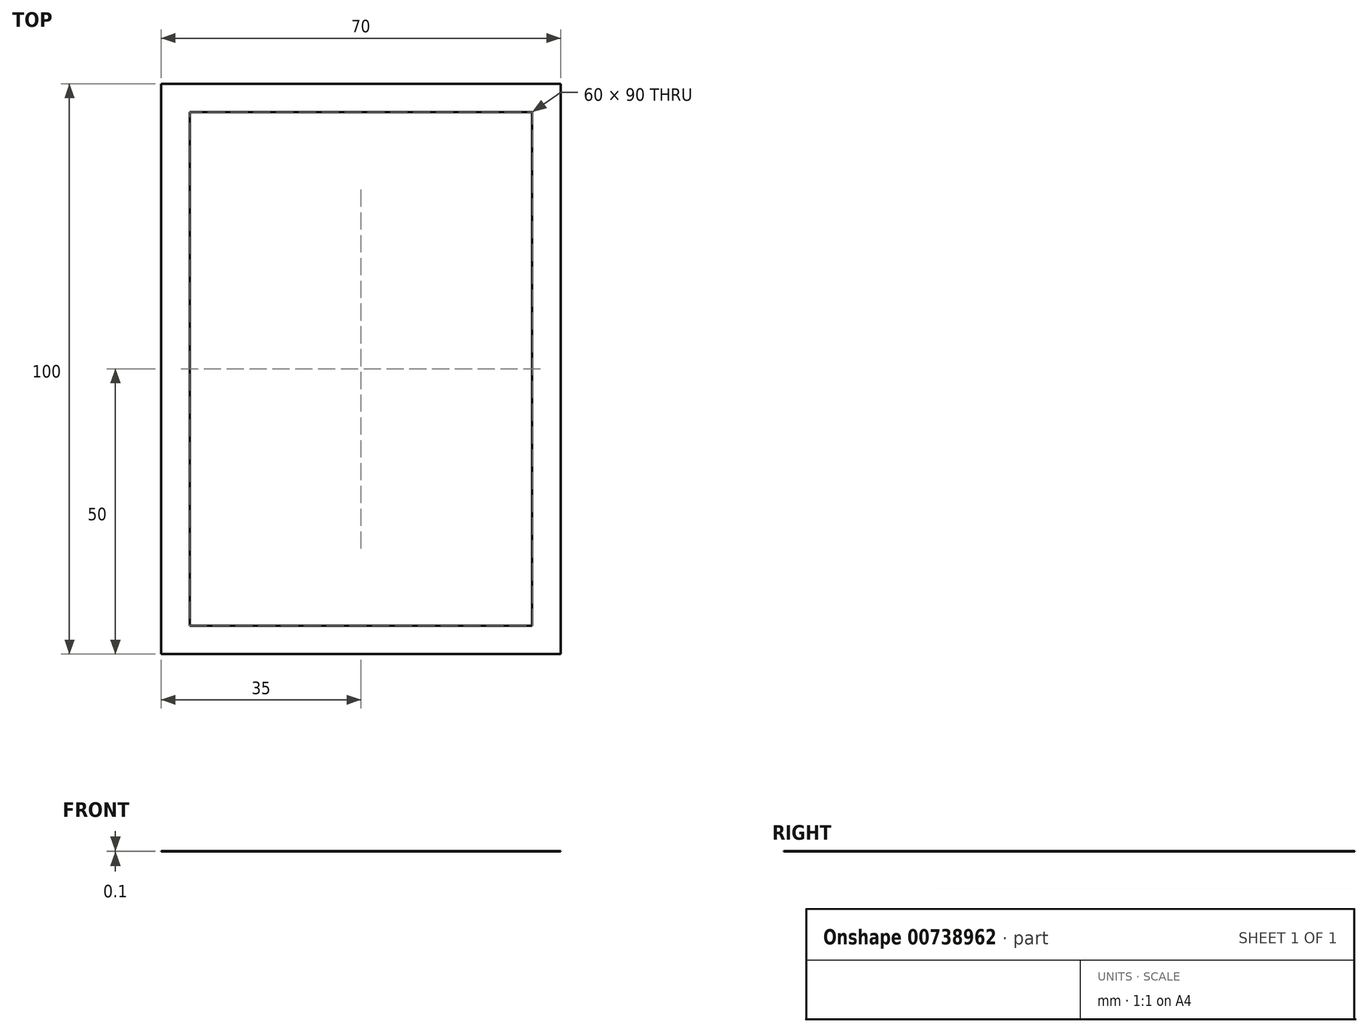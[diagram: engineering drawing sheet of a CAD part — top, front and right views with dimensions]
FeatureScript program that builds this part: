
annotation { "Feature Type Name" : "Feature", "Feature Type Description" : "" }
export const myFeature = defineFeature(function(context is Context, id is Id, definition is map)
    precondition{}
    {
        {
            var Q0;
            Q0=qCreatedBy(makeId("Top.planeOp"),FACE);
            var sketch = newSketch(context, id + "F0", { "sketchPlane" : qUnion([Q0])});
            skLineSegment(sketch, "E0.bottom", {"start": v(35, 50) * mm, "end": v(-35, 50) * mm});
            skLineSegment(sketch, "E0.top", {"start": v(35, -50) * mm, "end": v(-35, -50) * mm});
            skLineSegment(sketch, "E0.left", {"start": v(35, 50) * mm, "end": v(35, -50) * mm});
            skLineSegment(sketch, "E0.right", {"start": v(-35, 50) * mm, "end": v(-35, -50) * mm});
            skPoint(sketch, "E0.middle", {"position": v(0, 0) * mm});
            skLineSegment(sketch, "E1.0", {"start": v(-30, 45) * mm, "end": v(-30, -45) * mm});
            skLineSegment(sketch, "E1.1", {"start": v(30, 45) * mm, "end": v(-30, 45) * mm});
            skLineSegment(sketch, "E1.2", {"start": v(30, 45) * mm, "end": v(30, -45) * mm});
            skLineSegment(sketch, "E1.3", {"start": v(30, -45) * mm, "end": v(-30, -45) * mm});
            skSolve(sketch);
        }
        {
            var Q0;
            Q0=makeQuery(id+"F0.imprint","IMPRINT",FACE,{"disambiguationData":[TD([[makeQuery(id+"F0.imprint","IMPRINT",EDGE,{"derivedFrom":sQuery(id+"F0.wireOp",EDGE,"E0.bottom")}),1.0]])]});
            extrude(context, id + "F1", {"entities" : qUnion([Q0]), "depth" : .1 * mm, "offsetDistance" : 25 * mm});
        }
    });
